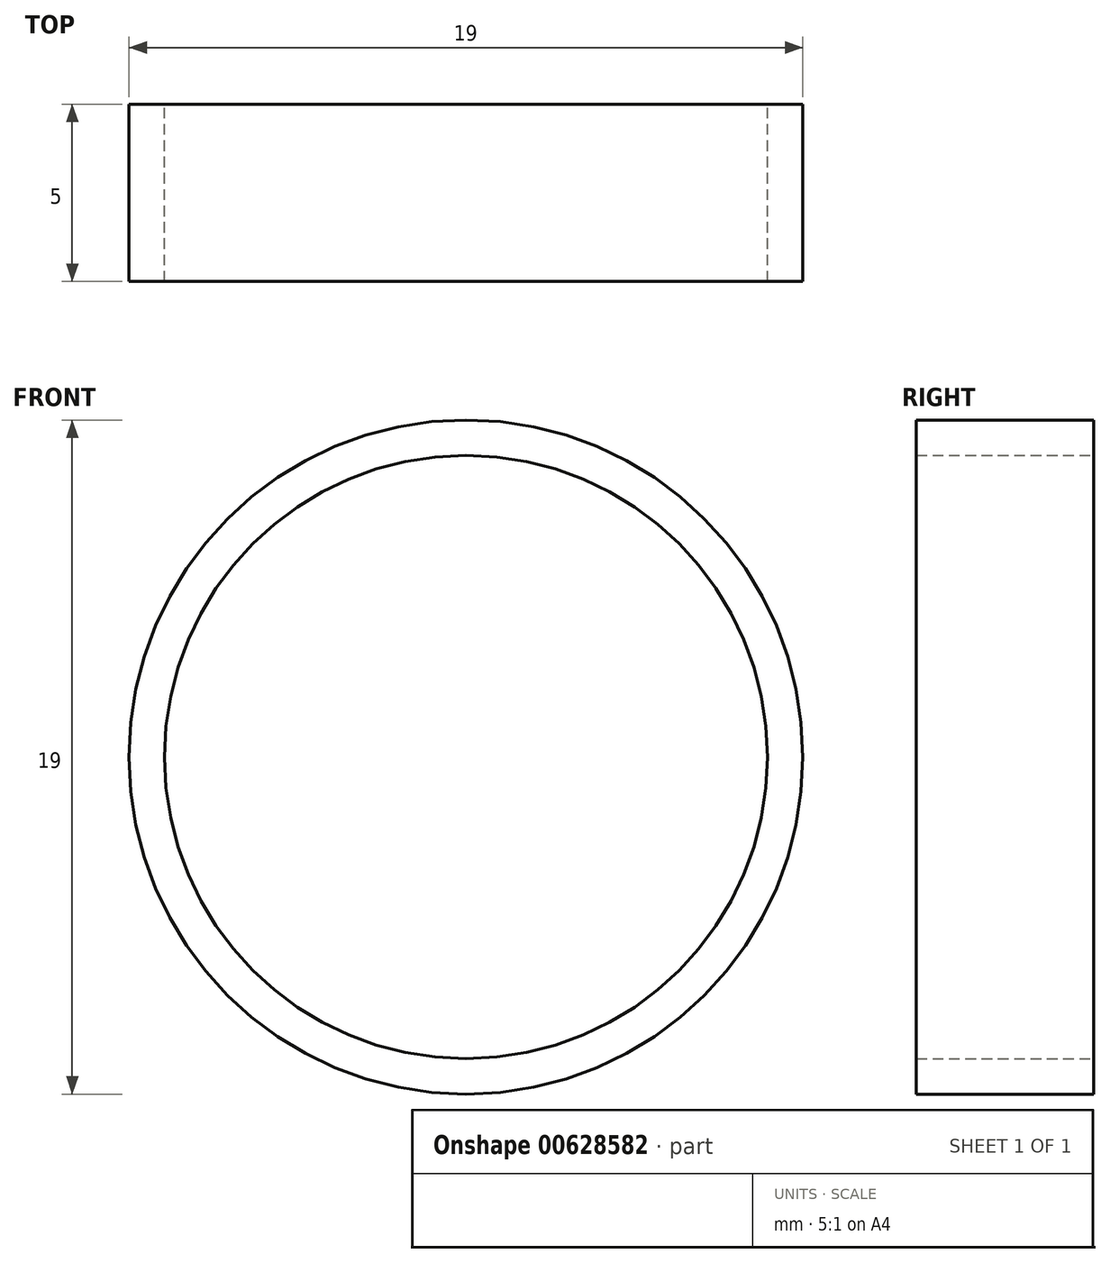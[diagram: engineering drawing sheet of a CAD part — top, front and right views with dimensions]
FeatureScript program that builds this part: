
annotation { "Feature Type Name" : "Feature", "Feature Type Description" : "" }
export const myFeature = defineFeature(function(context is Context, id is Id, definition is map)
    precondition{}
    {
        {
            var Q0;
            Q0=qCreatedBy(makeId("Front.planeOp"),FACE);
            var sketch = newSketch(context, id + "F0", { "sketchPlane" : qUnion([Q0])});
            skCircle(sketch, "E0", {"center": v(0, 0) * mm, "radius": 8.5 * mm});
            skCircle(sketch, "E1", {"center": v(0, 0) * mm, "radius": 9.5 * mm});
            skSolve(sketch);
        }
        {
            var Q0;
            Q0=makeQuery(id+"F0.imprint","IMPRINT",FACE,{"disambiguationData":[TD([[makeQuery(id+"F0.imprint","IMPRINT",EDGE,{"derivedFrom":sQuery(id+"F0.wireOp",EDGE,"E0")}),-1.0]])]});
            extrude(context, id + "F1", {"entities" : qUnion([Q0]), "endBound" : BoundingType.SYMMETRIC, "depth" : 5 * mm, "offsetDistance" : 25.4 * mm});
        }
        {
            var Q0;
            Q0=qCreatedBy(makeId("Top.planeOp"),FACE);
            cPlane(context, id + "F2", {"entities" : qUnion([Q0]), "cplaneType" : CPlaneType.OFFSET, "offset" : 19 / 2 * mm, "width" : 152.4 * mm, "height" : 152.4 * mm});
        }
    });
